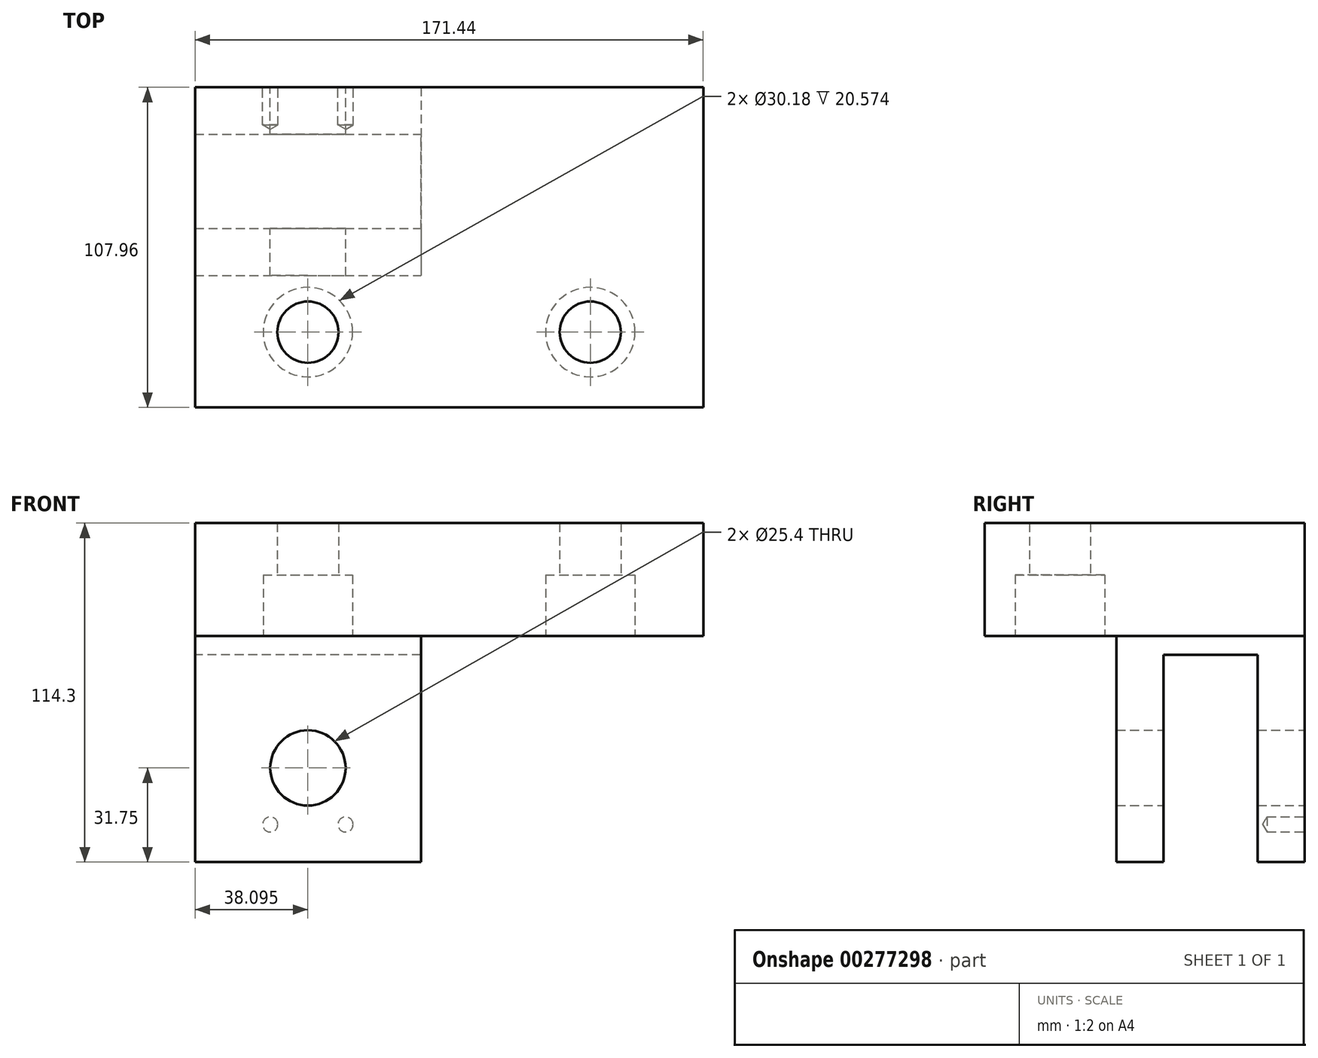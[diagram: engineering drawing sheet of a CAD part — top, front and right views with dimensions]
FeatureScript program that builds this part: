
annotation { "Feature Type Name" : "Feature", "Feature Type Description" : "" }
export const myFeature = defineFeature(function(context is Context, id is Id, definition is map)
    precondition{}
    {
        {
            var Q0;
            Q0=qCreatedBy(makeId("Top.planeOp"),FACE);
            var sketch = newSketch(context, id + "F0", { "sketchPlane" : qUnion([Q0])});
            skLineSegment(sketch, "E0.bottom", {"start": v(-85.73, 53.98) * mm, "end": v(85.73, 53.98) * mm});
            skLineSegment(sketch, "E0.top", {"start": v(-85.73, -53.98) * mm, "end": v(85.72, -53.98) * mm});
            skLineSegment(sketch, "E0.left", {"start": v(-85.73, 53.98) * mm, "end": v(-85.73, -53.98) * mm});
            skLineSegment(sketch, "E0.right", {"start": v(85.73, 53.97) * mm, "end": v(85.72, -53.98) * mm});
            skPoint(sketch, "E0.middle", {"position": v(0, 0) * mm});
            skSolve(sketch);
        }
        {
            var Q0;
            Q0 = qSketchRegion(id + "F0", true);
            extrude(context, id + "F1", {"entities" : qUnion([Q0]), "depth" : 38.1 * mm});
        }
        {
            var Q0;
            Q0=makeQuery(id+"F1.opExtrude","CAP_FACE",FACE,{"disambiguationData":[OSD([sQuery(id+"F0.wireOp",EDGE,"E0.bottom"),sQuery(id+"F0.wireOp",EDGE,"E0.top"),sQuery(id+"F0.wireOp",EDGE,"E0.left"),sQuery(id+"F0.wireOp",EDGE,"E0.right")])],"isStart":true});
            var sketch = newSketch(context, id + "F2", { "sketchPlane" : qUnion([Q0])});
            skLineSegment(sketch, "E1.0", {"start": v(-85.73, -22.23) * mm, "end": v(85.73, -22.23) * mm, "construction": true});
            skLineSegment(sketch, "E2.0", {"start": v(-85.73, 28.58) * mm, "end": v(85.73, 28.58) * mm, "construction": true});
            skLineSegment(sketch, "E3.bottom", {"start": v(-85.73, -53.98) * mm, "end": v(-9.53, -53.98) * mm});
            skLineSegment(sketch, "E3.top", {"start": v(-85.73, 9.52) * mm, "end": v(-9.53, 9.52) * mm});
            skLineSegment(sketch, "E3.left", {"start": v(-85.73, -53.98) * mm, "end": v(-85.73, 9.53) * mm});
            skLineSegment(sketch, "E3.right", {"start": v(-9.53, -53.98) * mm, "end": v(-9.53, 9.52) * mm});
            skLineSegment(sketch, "E4.0", {"start": v(47.63, -53.98) * mm, "end": v(47.62, 53.97) * mm, "construction": true});
            skLineSegment(sketch, "E5.0", {"start": v(-47.63, -53.98) * mm, "end": v(-47.63, 53.97) * mm, "construction": true});
            skPoint(sketch, "E6", {"position": v(-47.63, 28.58) * mm});
            skPoint(sketch, "E7", {"position": v(47.62, 28.58) * mm});
            skSolve(sketch);
        }
        {
            var Q0;
            Q0=sQuery(id+"F2.wireOp",VERTEX,"E6");
            var Q1;
            Q1=sQuery(id+"F2.wireOp",VERTEX,"E7");
            var Q2;
            Q2=makeQuery(id+"F1.opExtrude","SWEPT_BODY",BODY,{"disambiguationData":[OSD([sQuery(id+"F0.wireOp",EDGE,"E0.bottom"),sQuery(id+"F0.wireOp",EDGE,"E0.top"),sQuery(id+"F0.wireOp",EDGE,"E0.left"),sQuery(id+"F0.wireOp",EDGE,"E0.right")])]});
            hole(context, id + "F3", {"style" : HoleStyle.C_BORE, "endStyle" : HoleEndStyle.THROUGH, "holeDiameter" : 20.64 * mm, "cBoreDiameter" : 30.18 * mm, "cBoreDepth" : 20.57 * mm, "tappedDepth" : 20.62 * mm, "tapClearance" : 3, "startFromSketch" : true, "locations" : qUnion([Q0, Q1]), "scope" : qUnion([Q2])});
        }
        {
            var Q0;
            Q0=makeQuery(id+"F2.imprint","IMPRINT",FACE,{"disambiguationData":[TD([[makeQuery(id+"F2.imprint","IMPRINT",EDGE,{"derivedFrom":sQuery(id+"F2.wireOp",EDGE,"E3.bottom")}),1.0]])]});
            extrude(context, id + "F4", {"entities" : qUnion([Q0]), "operationType" : NewBodyOperationType.ADD, "depth" : 76.2 * mm});
        }
        {
            var Q0;
            Q0=makeQuery(id+"F4.boolean.opBoolean","MERGE",FACE,{"derivedFrom":[makeQuery(id+"F1.opExtrude","SWEPT_FACE",FACE,{"disambiguationData":[OSD([sQuery(id+"F0.wireOp",EDGE,"E0.left")])]}),makeQuery(id+"F4.opExtrude","SWEPT_FACE",FACE,{"disambiguationData":[OSD([sQuery(id+"F2.wireOp",EDGE,"E3.left")])]})]});
            var sketch = newSketch(context, id + "F5", { "sketchPlane" : qUnion([Q0])});
            skLineSegment(sketch, "E8.0", {"start": v(-53.97, -76.2) * mm, "end": v(9.53, -76.2) * mm, "construction": true});
            skLineSegment(sketch, "E9", {"start": v(-22.22, -76.2) * mm, "end": v(-22.22, -11.04) * mm, "construction": true});
            skLineSegment(sketch, "E10.bottom", {"start": v(-6.35, -6.35) * mm, "end": v(-38.1, -6.35) * mm});
            skLineSegment(sketch, "E10.top", {"start": v(-6.35, -146.05) * mm, "end": v(-38.1, -146.05) * mm});
            skLineSegment(sketch, "E10.left", {"start": v(-6.35, -6.35) * mm, "end": v(-6.35, -146.05) * mm});
            skLineSegment(sketch, "E10.right", {"start": v(-38.1, -6.35) * mm, "end": v(-38.1, -146.05) * mm});
            skPoint(sketch, "E10.middle", {"position": v(-22.22, -76.2) * mm});
            skSolve(sketch);
        }
        {
            var Q0;
            Q0 = qSketchRegion(id + "F5", true);
            extrude(context, id + "F6", {"entities" : qUnion([Q0]), "operationType" : NewBodyOperationType.REMOVE, "endBound" : BoundingType.THROUGH_ALL, "oppositeDirection" : true, "depth" : 25.4 * mm});
        }
        {
            var Q0;
            Q0=makeQuery(id+"F4.boolean.opBoolean","MERGE",FACE,{"derivedFrom":[makeQuery(id+"F1.opExtrude","SWEPT_FACE",FACE,{"disambiguationData":[OSD([sQuery(id+"F0.wireOp",EDGE,"E0.bottom")])]}),makeQuery(id+"F4.opExtrude","SWEPT_FACE",FACE,{"disambiguationData":[OSD([sQuery(id+"F2.wireOp",EDGE,"E3.bottom")])]})]});
            var sketch = newSketch(context, id + "F7", { "sketchPlane" : qUnion([Q0])});
            skLineSegment(sketch, "E11.0", {"start": v(9.53, -76.2) * mm, "end": v(9.53, 0) * mm, "construction": true});
            skLineSegment(sketch, "E12", {"start": v(9.53, 0) * mm, "end": v(47.63, 0) * mm, "construction": true});
            skLineSegment(sketch, "E13", {"start": v(47.63, 0) * mm, "end": v(47.63, -44.45) * mm, "construction": true});
            skPoint(sketch, "E14", {"position": v(47.63, -44.45) * mm});
            skSolve(sketch);
        }
        {
            var Q0;
            Q0=sQuery(id+"F7.wireOp",VERTEX,"E14");
            var Q1;
            Q1=makeQuery(id+"F1.opExtrude","SWEPT_BODY",BODY,{"disambiguationData":[OSD([sQuery(id+"F0.wireOp",EDGE,"E0.bottom"),sQuery(id+"F0.wireOp",EDGE,"E0.top"),sQuery(id+"F0.wireOp",EDGE,"E0.left"),sQuery(id+"F0.wireOp",EDGE,"E0.right")])]});
            hole(context, id + "F8", {"style" : HoleStyle.SIMPLE, "endStyle" : HoleEndStyle.THROUGH, "standardTappedOrClearance" : lookupTablePath({ "standard" : "ANSI", "size" : "1 (1)", "type" : "Drilled" }), "standardBlindInLast" : lookupTablePath({ "standard" : "ANSI", "size" : "1", "type" : "Drilled" }), "holeDiameter" : 25.4 * mm, "tappedDepth" : 20.62 * mm, "tapClearance" : 3, "startFromSketch" : true, "locations" : qUnion([Q0]), "scope" : qUnion([Q1])});
        }
        {
            var Q0;
            Q0=makeQuery(id+"F4.boolean.opBoolean","MERGE",FACE,{"derivedFrom":[makeQuery(id+"F1.opExtrude","SWEPT_FACE",FACE,{"disambiguationData":[OSD([sQuery(id+"F0.wireOp",EDGE,"E0.bottom")])]}),makeQuery(id+"F4.opExtrude","SWEPT_FACE",FACE,{"disambiguationData":[OSD([sQuery(id+"F2.wireOp",EDGE,"E3.bottom")])]})]});
            var sketch = newSketch(context, id + "F9", { "sketchPlane" : qUnion([Q0])});
            skCircle(sketch, "E15.0", {"center": v(47.63, -44.45) * mm, "radius": 12.7 * mm, "construction": true});
            skLineSegment(sketch, "E16", {"start": v(47.63, -44.45) * mm, "end": v(47.63, -63.5) * mm, "construction": true});
            skLineSegment(sketch, "E17", {"start": v(47.63, -63.5) * mm, "end": v(34.93, -63.5) * mm, "construction": true});
            skPoint(sketch, "E18", {"position": v(34.93, -63.5) * mm});
            skPoint(sketch, "E19.MirrorP", {"position": v(60.33, -63.5) * mm});
            skSolve(sketch);
        }
        {
            var Q0;
            Q0=sQuery(id+"F9.wireOp",VERTEX,"E18");
            var Q1;
            Q1=sQuery(id+"F9.wireOp",VERTEX,"E19.MirrorP");
            var Q2;
            Q2=makeQuery(id+"F1.opExtrude","SWEPT_BODY",BODY,{"disambiguationData":[OSD([sQuery(id+"F0.wireOp",EDGE,"E0.bottom"),sQuery(id+"F0.wireOp",EDGE,"E0.top"),sQuery(id+"F0.wireOp",EDGE,"E0.left"),sQuery(id+"F0.wireOp",EDGE,"E0.right")])]});
            hole(context, id + "F10", {"style" : HoleStyle.SIMPLE, "endStyle" : HoleEndStyle.BLIND, "standardTappedOrClearance" : lookupTablePath({ "standard" : "ANSI", "engagement" : "75%", "pitch" : "20 tpi", "size" : "1/4", "type" : "Tapped" }), "standardBlindInLast" : lookupTablePath({ "standard" : "ANSI", "engagement" : "75%", "pitch" : "20 tpi", "size" : "1/4", "type" : "Tapped" }), "holeDiameter" : 5.1 * mm, "showTappedDepth" : true, "holeDepth" : 12.7 * mm, "tappedDepth" : 8.9 * mm, "tapClearance" : 3, "startFromSketch" : true, "locations" : qUnion([Q0, Q1]), "scope" : qUnion([Q2]), "majorDiameter" : 6.35 * mm});
        }
    });
